# Revit family: Shower-Showerhead-KALLISTA-Vice-P34593
name_source: partatom
category: Plumbing Fixtures
units: mm (PartAtom-declared; Revit-internal decimal feet)

## family parameters
Cut with Voids When Loaded = No
Host = Face
OmniClass Number = 23.31.17.00
OmniClass Title = Showers
Part Type = Normal
Room Calculation Point = No
Round Connector Dimension = Use Diameter
Shared = No

## types (5) — shared parameters
ADA Compliant = No
Assembly Code = D2010700
CW Connection = Yes
Cold Water Inlet = Cold Water Inlet
Date Modified = 05/26/2024
Default Elevation = 42"
Description = Showerhead
Drain Included = No
Flow Rate = 3 GPM
HW Connection = Yes
Height = 6 11/16"
Hot Water Inlet = Hot Water Inlet
Length = 6 3/4"
Manufacturer = Kallista Co.
Master Format 2014 = 22 42 23
Master Format 2014 Name = Residential Showers
Material = Premium Metal Construction
Pressure = 45.00 psi
Product Name = Vice
Tempered Water Inlet = Tempered Water Inlet
URL = https://www.kallista.com
Vent Connection = No
Waste Connection = No
Waste Water Outlet = Waste Water Outlet
WaterSense Certified = No
Width = 5 7/8"

## per-type parameters (varying)
| type | Finish | Model | Secondary Finish | Type |
| Bruhsed Bronze Sprayface, CP-Chrome | Kallista-Metal-CP-Chrome | P34593-BV-CP | Kallista-Metal-BV-Brushed_Bronze | 4 |
| Bruhsed French Gold Sprayface, AF-French Gold | Kallista-Metal-AF-French_Gold | P34593-BAF-AF | Kallista-Metal-BAF-Brushed_French_Gold | 1 |
| Chrome Sprayface, CP-Chrome | Kallista-Metal-CP-Chrome | P34593-CP-CP | Kallista-Metal-CP-Chrome | 5 |
| Vibrant Bruhsed Nickel Sprayface, BGP | Kallista-Metal-BGP | P34593-BN-BGP | Kallista-Metal-BN-Brushed_Nickel | 2 |
| Vibrant Bruhsed Nickel Sprayface, SN-Polished Nickel | Kallista-Metal-SN-Polished_Nickel | P34593-BN-SN | Kallista-Metal-BN-Brushed_Nickel | 3 |

## geometry (parser evidence)
native form markers: Sweep x6
no freeform markers — native parametric forms only
